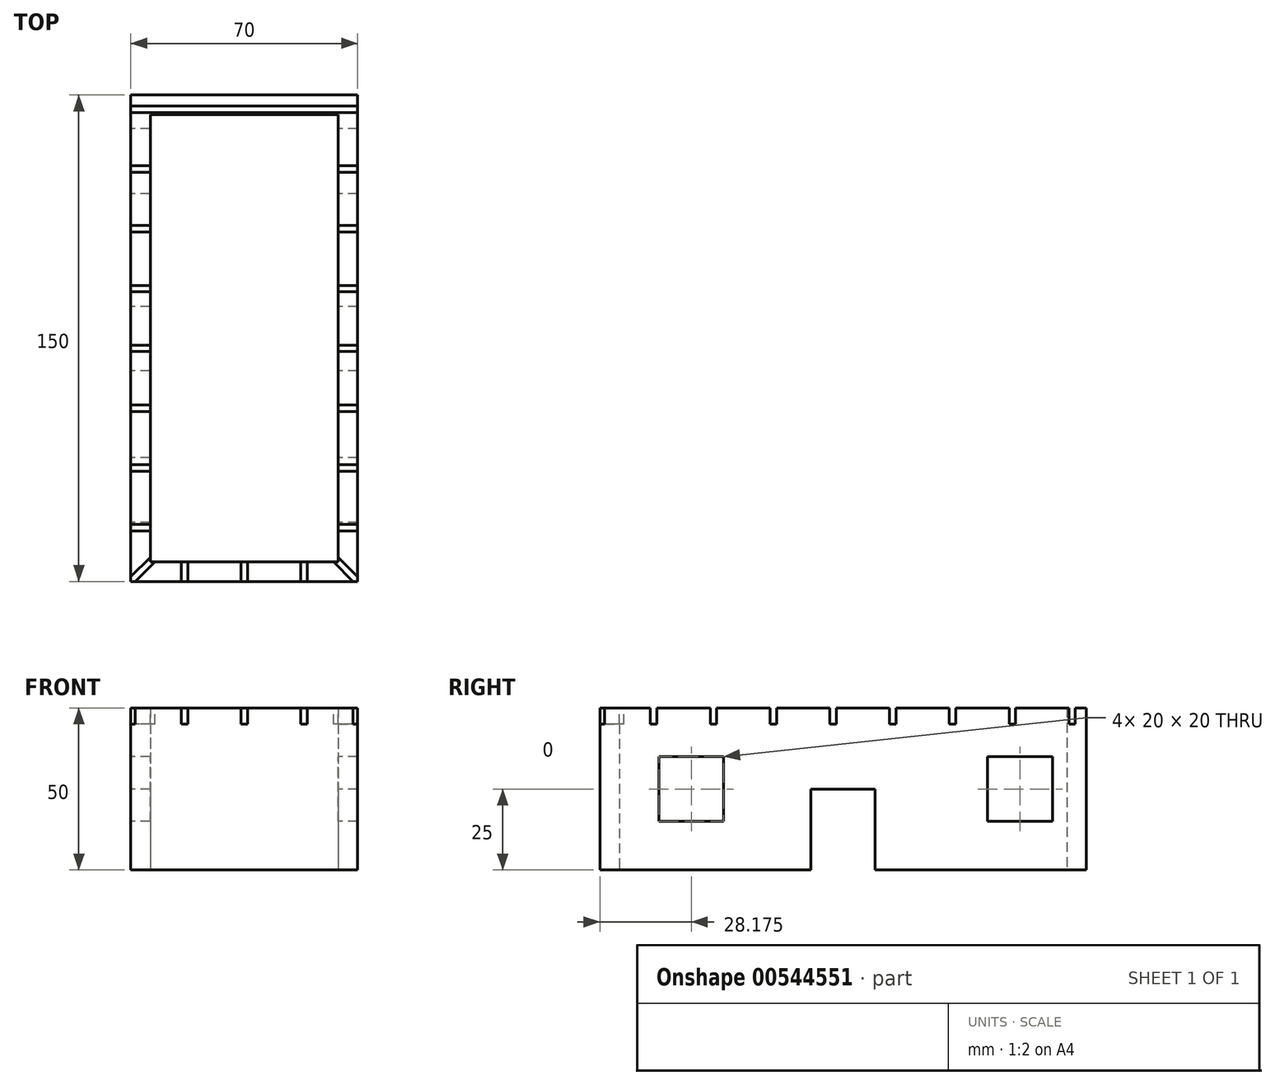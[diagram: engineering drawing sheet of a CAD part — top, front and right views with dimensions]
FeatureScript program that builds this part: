
annotation { "Feature Type Name" : "Feature", "Feature Type Description" : "" }
export const myFeature = defineFeature(function(context is Context, id is Id, definition is map)
    precondition{}
    {
        {
            var Q0;
            Q0=qCreatedBy(makeId("Top.planeOp"),FACE);
            var sketch = newSketch(context, id + "F0", { "sketchPlane" : qUnion([Q0])});
            skLineSegment(sketch, "E0.bottom", {"start": v(35, 75) * mm, "end": v(-35, 75) * mm});
            skLineSegment(sketch, "E0.top", {"start": v(35, -75) * mm, "end": v(-35, -75) * mm});
            skLineSegment(sketch, "E0.left", {"start": v(35, 75) * mm, "end": v(35, -75) * mm});
            skLineSegment(sketch, "E0.right", {"start": v(-35, 75) * mm, "end": v(-35, -75) * mm});
            skPoint(sketch, "E0.middle", {"position": v(0, 0) * mm});
            skLineSegment(sketch, "E1.0", {"start": v(29, 69) * mm, "end": v(-29, 69) * mm});
            skLineSegment(sketch, "E1.1", {"start": v(29, 69) * mm, "end": v(29, -69) * mm});
            skLineSegment(sketch, "E1.2", {"start": v(29, -69) * mm, "end": v(-29, -69) * mm});
            skLineSegment(sketch, "E1.3", {"start": v(-29, 69) * mm, "end": v(-29, -69) * mm});
            skSolve(sketch);
        }
        {
            var Q0;
            Q0 = qSketchRegion(id + "F0", true);
            extrude(context, id + "F1", {"entities" : qUnion([Q0]), "depth" : 50 * mm, "offsetDistance" : 25 * mm});
        }
        {
            var Q0;
            Q0=makeQuery(id+"F1.opExtrude","CAP_FACE",FACE,{"disambiguationData":[OSD([sQuery(id+"F0.wireOp",EDGE,"E0.bottom"),sQuery(id+"F0.wireOp",EDGE,"E0.top"),sQuery(id+"F0.wireOp",EDGE,"E0.left"),sQuery(id+"F0.wireOp",EDGE,"E0.right"),sQuery(id+"F0.wireOp",EDGE,"E1.0"),sQuery(id+"F0.wireOp",EDGE,"E1.1"),sQuery(id+"F0.wireOp",EDGE,"E1.2"),sQuery(id+"F0.wireOp",EDGE,"E1.3")])],"isStart":false});
            var sketch = newSketch(context, id + "F2", { "sketchPlane" : qUnion([Q0])});
            skLineSegment(sketch, "E2.0", {"start": v(1, -75) * mm, "end": v(1, -69) * mm});
            skLineSegment(sketch, "E3.0", {"start": v(-1, -75) * mm, "end": v(-1, -69) * mm});
            skLineSegment(sketch, "E4.0", {"start": v(-28.3, -69.7) * mm, "end": v(-34.3, -75.7) * mm});
            skLineSegment(sketch, "E5.0", {"start": v(-29.7, -68.3) * mm, "end": v(-35.7, -74.3) * mm});
            skLineSegment(sketch, "E6.0", {"start": v(28.3, -69.7) * mm, "end": v(33.59, -75) * mm});
            skLineSegment(sketch, "E7.0", {"start": v(29.7, -68.3) * mm, "end": v(35, -73.59) * mm});
            skLineSegment(sketch, "E8", {"start": v(28.3, -69.7) * mm, "end": v(27.59, -69) * mm});
            skLineSegment(sketch, "E9", {"start": v(29.7, -68.3) * mm, "end": v(29, -67.59) * mm});
            skLineSegment(sketch, "E10", {"start": v(-28.3, -69.7) * mm, "end": v(-27.59, -69) * mm});
            skLineSegment(sketch, "E11", {"start": v(-29.7, -68.3) * mm, "end": v(-29, -67.59) * mm});
            skPoint(sketch, "E12.end.orphan", {"position": v(0, -69) * mm});
            skPoint(sketch, "E12.start.orphan", {"position": v(0, -75) * mm});
            skLineSegment(sketch, "E13", {"start": v(-29, -67.59) * mm, "end": v(-29, -69) * mm});
            skLineSegment(sketch, "E14", {"start": v(35, -73.59) * mm, "end": v(35, -75) * mm});
            skLineSegment(sketch, "E15", {"start": v(35, -75) * mm, "end": v(33.59, -75) * mm});
            skLineSegment(sketch, "E16", {"start": v(27.59, -69) * mm, "end": v(29, -67.59) * mm});
            skLineSegment(sketch, "E17", {"start": v(-1, -69) * mm, "end": v(1, -69) * mm});
            skLineSegment(sketch, "E18", {"start": v(1, -75) * mm, "end": v(-1, -75) * mm});
            skLineSegment(sketch, "E19", {"start": v(-29, -67.59) * mm, "end": v(-27.59, -69) * mm});
            skLineSegment(sketch, "E20", {"start": v(-35.7, -74.3) * mm, "end": v(-34.3, -75.7) * mm});
            skSolve(sketch);
        }
        {
            var Q0;
            Q0 = qSketchRegion(id + "F2", true);
            extrude(context, id + "F3", {"entities" : qUnion([Q0]), "operationType" : NewBodyOperationType.REMOVE, "oppositeDirection" : true, "depth" : 5 * mm, "offsetDistance" : 25 * mm});
        }
        {
            var Q0;
            {var subQ0=sQuery(id+"F0.wireOp",EDGE,"E0.top");var subQ1=sQuery(id+"F0.wireOp",EDGE,"E1.2");Q0=makeQuery(id+"F3.boolean.opBoolean","SPLIT",FACE,{"disambiguationData":[TD([makeQuery(id+"F3.opExtrude","SWEPT_FACE",FACE,{"disambiguationData":[OSD([sQuery(id+"F2.wireOp",EDGE,"E3.0")])]})])],"derivedFrom":makeQuery(id+"F1.opExtrude","CAP_FACE",FACE,{"disambiguationData":[OSD([sQuery(id+"F0.wireOp",EDGE,"E0.bottom"),subQ0,sQuery(id+"F0.wireOp",EDGE,"E0.left"),sQuery(id+"F0.wireOp",EDGE,"E0.right"),sQuery(id+"F0.wireOp",EDGE,"E1.0"),sQuery(id+"F0.wireOp",EDGE,"E1.1"),subQ1,sQuery(id+"F0.wireOp",EDGE,"E1.3")])],"isStart":false})});}
            var sketch = newSketch(context, id + "F4", { "sketchPlane" : qUnion([Q0])});
            skLineSegment(sketch, "E21.0", {"start": v(-19.44, -69) * mm, "end": v(-19.44, -75) * mm});
            skLineSegment(sketch, "E22.0", {"start": v(-17.44, -69) * mm, "end": v(-17.44, -75) * mm});
            skLineSegment(sketch, "E23.MirrorCS", {"start": v(17.44, -69) * mm, "end": v(17.44, -75) * mm});
            skLineSegment(sketch, "E24.MirrorCS", {"start": v(19.44, -69) * mm, "end": v(19.44, -75) * mm});
            skLineSegment(sketch, "E25", {"start": v(-19.44, -69) * mm, "end": v(-17.44, -69) * mm});
            skLineSegment(sketch, "E26", {"start": v(-19.44, -75) * mm, "end": v(-17.44, -75) * mm});
            skLineSegment(sketch, "E27", {"start": v(17.44, -69) * mm, "end": v(19.44, -69) * mm});
            skLineSegment(sketch, "E28", {"start": v(17.44, -75) * mm, "end": v(19.44, -75) * mm});
            skSolve(sketch);
        }
        {
            var Q0;
            Q0 = qSketchRegion(id + "F4", true);
            extrude(context, id + "F5", {"entities" : qUnion([Q0]), "operationType" : NewBodyOperationType.REMOVE, "oppositeDirection" : true, "depth" : 5 * mm, "offsetDistance" : 25 * mm});
        }
        {
            var Q0;
            {var subQ0=sQuery(id+"F0.wireOp",EDGE,"E1.0");var subQ1=sQuery(id+"F0.wireOp",EDGE,"E0.left");var subQ2=sQuery(id+"F0.wireOp",EDGE,"E0.right");var subQ3=sQuery(id+"F0.wireOp",EDGE,"E0.bottom");var subQ4=sQuery(id+"F0.wireOp",EDGE,"E1.1");var subQ5=sQuery(id+"F0.wireOp",EDGE,"E1.3");Q0=makeQuery(id+"F3.boolean.opBoolean","SPLIT",FACE,{"disambiguationData":[TD([makeQuery(id+"F1.opExtrude","SWEPT_FACE",FACE,{"disambiguationData":[OSD([subQ3])]})])],"derivedFrom":makeQuery(id+"F1.opExtrude","CAP_FACE",FACE,{"disambiguationData":[OSD([subQ3,sQuery(id+"F0.wireOp",EDGE,"E0.top"),subQ1,subQ2,subQ0,subQ4,sQuery(id+"F0.wireOp",EDGE,"E1.2"),subQ5])],"isStart":false})});}
            var sketch = newSketch(context, id + "F6", { "sketchPlane" : qUnion([Q0])});
            skLineSegment(sketch, "E29", {"start": v(35, -73.59) * mm, "end": v(35, -59.44) * mm});
            skLineSegment(sketch, "E30", {"start": v(35, -59.44) * mm, "end": v(29, -59.44) * mm});
            skLineSegment(sketch, "E31.0", {"start": v(35, -57.44) * mm, "end": v(29, -57.44) * mm});
            skLineSegment(sketch, "E32.0.1.0", {"start": v(35, -39) * mm, "end": v(29, -39) * mm});
            skLineSegment(sketch, "E32.0.1.1", {"start": v(35, -41) * mm, "end": v(29, -41) * mm});
            skLineSegment(sketch, "E32.0.2.0", {"start": v(35, -20.56) * mm, "end": v(29, -20.56) * mm});
            skLineSegment(sketch, "E32.0.2.1", {"start": v(35, -22.56) * mm, "end": v(29, -22.56) * mm});
            skLineSegment(sketch, "E32.0.3.0", {"start": v(35, -2.12) * mm, "end": v(29, -2.12) * mm});
            skLineSegment(sketch, "E32.0.3.1", {"start": v(35, -4.12) * mm, "end": v(29, -4.12) * mm});
            skLineSegment(sketch, "E32.0.4.0", {"start": v(35, 16.32) * mm, "end": v(29, 16.32) * mm});
            skLineSegment(sketch, "E32.0.4.1", {"start": v(35, 14.32) * mm, "end": v(29, 14.32) * mm});
            skLineSegment(sketch, "E32.0.5.0", {"start": v(35, 34.76) * mm, "end": v(29, 34.76) * mm});
            skLineSegment(sketch, "E32.0.5.1", {"start": v(35, 32.76) * mm, "end": v(29, 32.76) * mm});
            skLineSegment(sketch, "E32.0.6.0", {"start": v(35, 53.2) * mm, "end": v(29, 53.2) * mm});
            skLineSegment(sketch, "E32.0.6.1", {"start": v(35, 51.2) * mm, "end": v(29, 51.2) * mm});
            skLineSegment(sketch, "E32.0.7.0", {"start": v(35, 71.64) * mm, "end": v(29, 71.64) * mm});
            skLineSegment(sketch, "E32.0.7.1", {"start": v(35, 69.64) * mm, "end": v(29, 69.64) * mm});
            skLineSegment(sketch, "E32.direction1", {"start": v(29, -57.44) * mm, "end": v(54, -57.44) * mm, "construction": true});
            skLineSegment(sketch, "E32.direction2", {"start": v(29, -57.44) * mm, "end": v(29, -39) * mm, "construction": true});
            skLineSegment(sketch, "E33", {"start": v(29, 71.64) * mm, "end": v(-35, 71.64) * mm});
            skLineSegment(sketch, "E34", {"start": v(-35, 71.64) * mm, "end": v(-35, 69.64) * mm});
            skLineSegment(sketch, "E35", {"start": v(-35, 69.64) * mm, "end": v(29, 69.64) * mm});
            skLineSegment(sketch, "E36.bottom", {"start": v(35, 53.2) * mm, "end": v(-39.61, 53.2) * mm});
            skLineSegment(sketch, "E36.top", {"start": v(35, 51.2) * mm, "end": v(-39.61, 51.2) * mm});
            skLineSegment(sketch, "E36.left", {"start": v(35, 53.2) * mm, "end": v(35, 51.2) * mm});
            skLineSegment(sketch, "E36.right", {"start": v(-39.61, 53.2) * mm, "end": v(-39.61, 51.2) * mm});
            skLineSegment(sketch, "E37.bottom", {"start": v(35, 34.76) * mm, "end": v(-44, 34.76) * mm});
            skLineSegment(sketch, "E37.top", {"start": v(35, 32.76) * mm, "end": v(-44, 32.76) * mm});
            skLineSegment(sketch, "E37.left", {"start": v(35, 34.76) * mm, "end": v(35, 32.76) * mm});
            skLineSegment(sketch, "E37.right", {"start": v(-44, 34.76) * mm, "end": v(-44, 32.76) * mm});
            skPoint(sketch, "E38.oppositeSnap0", {"position": v(32, 14.32) * mm});
            skLineSegment(sketch, "E38.bottom", {"start": v(35, 16.32) * mm, "end": v(-44, 16.32) * mm});
            skLineSegment(sketch, "E38.top", {"start": v(35, 14.32) * mm, "end": v(-44, 14.32) * mm});
            skLineSegment(sketch, "E38.left", {"start": v(35, 16.32) * mm, "end": v(35, 14.32) * mm});
            skLineSegment(sketch, "E38.right", {"start": v(-44, 16.32) * mm, "end": v(-44, 14.32) * mm});
            skLineSegment(sketch, "E39.bottom", {"start": v(35, -2.12) * mm, "end": v(-41.4, -2.12) * mm});
            skLineSegment(sketch, "E39.top", {"start": v(35, -4.12) * mm, "end": v(-41.4, -4.12) * mm});
            skLineSegment(sketch, "E39.left", {"start": v(35, -2.12) * mm, "end": v(35, -4.12) * mm});
            skLineSegment(sketch, "E39.right", {"start": v(-41.4, -2.12) * mm, "end": v(-41.4, -4.12) * mm});
            skLineSegment(sketch, "E40.bottom", {"start": v(35, -20.56) * mm, "end": v(-41.18, -20.56) * mm});
            skLineSegment(sketch, "E40.top", {"start": v(35, -22.56) * mm, "end": v(-41.18, -22.56) * mm});
            skLineSegment(sketch, "E40.left", {"start": v(35, -20.56) * mm, "end": v(35, -22.56) * mm});
            skLineSegment(sketch, "E40.right", {"start": v(-41.18, -20.56) * mm, "end": v(-41.18, -22.56) * mm});
            skLineSegment(sketch, "E41.bottom", {"start": v(35, -39) * mm, "end": v(-40.7, -39) * mm});
            skLineSegment(sketch, "E41.top", {"start": v(35, -41) * mm, "end": v(-40.7, -41) * mm});
            skLineSegment(sketch, "E41.left", {"start": v(35, -39) * mm, "end": v(35, -41) * mm});
            skLineSegment(sketch, "E41.right", {"start": v(-40.7, -39) * mm, "end": v(-40.7, -41) * mm});
            skPoint(sketch, "E42.oppositeSnap0", {"position": v(32, -59.44) * mm});
            skLineSegment(sketch, "E42.bottom", {"start": v(35, -57.44) * mm, "end": v(-66.52, -57.44) * mm});
            skLineSegment(sketch, "E42.top", {"start": v(35, -59.44) * mm, "end": v(-66.52, -59.44) * mm});
            skLineSegment(sketch, "E42.left", {"start": v(35, -57.44) * mm, "end": v(35, -59.44) * mm});
            skLineSegment(sketch, "E42.right", {"start": v(-66.52, -57.44) * mm, "end": v(-66.52, -59.44) * mm});
            skSolve(sketch);
        }
        {
            var Q0;
            Q0 = qSketchRegion(id + "F6", true);
            var Q1;
            {var subQ0=sQuery(id+"F6.wireOp",EDGE,"E32.0.7.0");Q1=makeQuery(id+"F6.imprint","IMPRINT",FACE,{"disambiguationData":[TD([[makeQuery(id+"F6.imprint","IMPRINT",EDGE,{"derivedFrom":subQ0}),1.0]])]});}
            extrude(context, id + "F7", {"entities" : qUnion([Q0, Q1]), "operationType" : NewBodyOperationType.REMOVE, "oppositeDirection" : true, "depth" : 5 * mm, "offsetDistance" : 25 * mm});
        }
        {
            var Q0;
            Q0=makeQuery(id+"F1.opExtrude","SWEPT_FACE",FACE,{"disambiguationData":[OSD([sQuery(id+"F0.wireOp",EDGE,"E0.right")])]});
            var sketch = newSketch(context, id + "F8", { "sketchPlane" : qUnion([Q0])});
            skLineSegment(sketch, "E43.bottom", {"start": v(-44.6, 35) * mm, "end": v(-64.6, 35) * mm});
            skLineSegment(sketch, "E43.top", {"start": v(-44.6, 15) * mm, "end": v(-64.6, 15) * mm});
            skLineSegment(sketch, "E43.left", {"start": v(-44.6, 35) * mm, "end": v(-44.6, 15) * mm});
            skLineSegment(sketch, "E43.right", {"start": v(-64.6, 35) * mm, "end": v(-64.6, 15) * mm});
            skPoint(sketch, "E43.middle", {"position": v(-54.6, 25) * mm});
            skPoint(sketch, "E43.middle.positionSnap0", {"position": v(-75, 25) * mm});
            skPoint(sketch, "E43.centerSnap0", {"position": v(-75, 25) * mm});
            skPoint(sketch, "E44.middle", {"position": v(0, 25) * mm});
            skPoint(sketch, "E44.middle.positionSnap0", {"position": v(-44.6, 25) * mm});
            skPoint(sketch, "E44.centerSnap0", {"position": v(-44.6, 25) * mm});
            skLineSegment(sketch, "E45.bottom", {"start": v(56.83, 35) * mm, "end": v(36.83, 35) * mm});
            skLineSegment(sketch, "E45.top", {"start": v(56.83, 15) * mm, "end": v(36.83, 15) * mm});
            skLineSegment(sketch, "E45.left", {"start": v(56.83, 35) * mm, "end": v(56.83, 15) * mm});
            skLineSegment(sketch, "E45.right", {"start": v(36.83, 35) * mm, "end": v(36.83, 15) * mm});
            skPoint(sketch, "E45.middle", {"position": v(46.83, 25) * mm});
            skPoint(sketch, "E45.middle.positionSnap0", {"position": v(10, 25) * mm});
            skPoint(sketch, "E45.centerSnap0", {"position": v(10, 25) * mm});
            skLineSegment(sketch, "E46.bottom", {"start": v(-9.83, 0) * mm, "end": v(10, 0) * mm});
            skLineSegment(sketch, "E46.top", {"start": v(-9.83, 25) * mm, "end": v(10, 25) * mm});
            skLineSegment(sketch, "E46.left", {"start": v(-9.83, 0) * mm, "end": v(-9.83, 25) * mm});
            skLineSegment(sketch, "E46.right", {"start": v(10, 0) * mm, "end": v(10, 25) * mm});
            skSolve(sketch);
        }
        {
            var Q0;
            Q0 = qSketchRegion(id + "F8", true);
            extrude(context, id + "F9", {"entities" : qUnion([Q0]), "operationType" : NewBodyOperationType.REMOVE, "oppositeDirection" : true, "depth" : 200 * mm, "offsetDistance" : 25 * mm});
        }
        {
            var Q0;
            Q0 = qSketchRegion(id + "F8", true);
            extrude(context, id + "F10", {"entities" : qUnion([Q0]), "operationType" : NewBodyOperationType.REMOVE, "oppositeDirection" : true, "depth" : 25 * mm, "offsetDistance" : 25 * mm});
        }
    });
